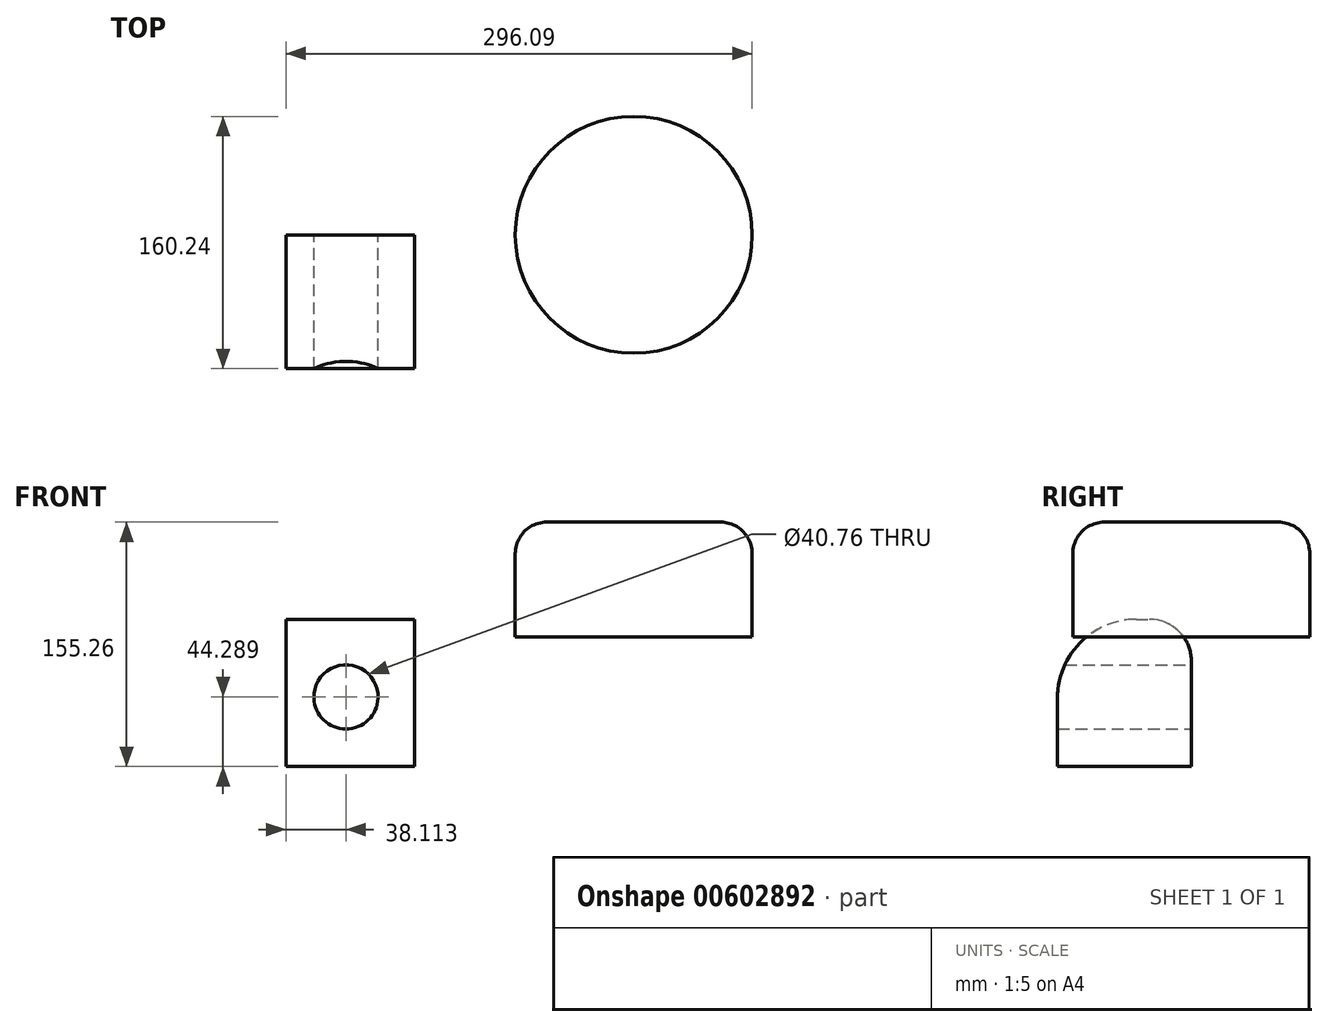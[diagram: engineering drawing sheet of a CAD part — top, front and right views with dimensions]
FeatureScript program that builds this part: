
annotation { "Feature Type Name" : "Feature", "Feature Type Description" : "" }
export const myFeature = defineFeature(function(context is Context, id is Id, definition is map)
    precondition{}
    {
        {
            var Q0;
            Q0=qCreatedBy(makeId("Top.planeOp"),FACE);
            var sketch = newSketch(context, id + "F0", { "sketchPlane" : qUnion([Q0])});
            skCircle(sketch, "E0", {"center": v(0, 0) * mm, "radius": 75.24 * mm});
            skSolve(sketch);
        }
        {
            var Q0;
            Q0=makeQuery(id+"F0.imprint","IMPRINT",FACE,{"disambiguationData":[TD([[makeQuery(id+"F0.imprint","IMPRINT",EDGE,{"derivedFrom":sQuery(id+"F0.wireOp",EDGE,"E0")}),1.0]])]});
            var Q1;
            Q1=sQuery(id+"F0.wireOp",EDGE,"E0");
            extrude(context, id + "F1", {"entities" : qUnion([Q0]), "surfaceEntities" : qUnion([Q1]), "depth" : 73 * mm, "offsetDistance" : 25 * mm});
        }
        {
            var Q0;
            Q0=qCreatedBy(makeId("Front.planeOp"),FACE);
            var sketch = newSketch(context, id + "F2", { "sketchPlane" : qUnion([Q0])});
            skLineSegment(sketch, "E1.bottom", {"start": v(-139.36, 11.27) * mm, "end": v(-220.85, 11.27) * mm});
            skLineSegment(sketch, "E1.top", {"start": v(-139.36, -82.26) * mm, "end": v(-220.85, -82.26) * mm});
            skLineSegment(sketch, "E1.left", {"start": v(-139.36, 11.27) * mm, "end": v(-139.36, -82.26) * mm});
            skLineSegment(sketch, "E1.right", {"start": v(-220.85, 11.27) * mm, "end": v(-220.85, -82.26) * mm});
            skCircle(sketch, "E2", {"center": v(-182.74, -37.97) * mm, "radius": 20.38 * mm});
            skSolve(sketch);
        }
        {
            var Q0;
            Q0=makeQuery(id+"F2.imprint","IMPRINT",FACE,{"disambiguationData":[TD([[makeQuery(id+"F2.imprint","IMPRINT",EDGE,{"derivedFrom":sQuery(id+"F2.wireOp",EDGE,"E1.bottom")}),1.0]])]});
            extrude(context, id + "F3", {"entities" : qUnion([Q0]), "depth" : 85 * mm, "offsetDistance" : 25 * mm});
        }
        {
            var Q0;
            Q0=makeQuery(id+"F3.opExtrude","CAP_EDGE",EDGE,{"disambiguationData":[OSD([sQuery(id+"F2.wireOp",EDGE,"E1.bottom")])],"isStart":false});
            fillet(context, id + "F4", {"entities" : qUnion([Q0]), "radius" : 50 * mm, "tangentPropagation" : true, "allowEdgeOverflow" : false});
        }
        {
            var Q0;
            Q0=makeQuery(id+"F3.opExtrude","CAP_EDGE",EDGE,{"disambiguationData":[OSD([sQuery(id+"F2.wireOp",EDGE,"E1.bottom")])],"isStart":true});
            fillet(context, id + "F5", {"entities" : qUnion([Q0]), "radius" : 26.56 * mm, "tangentPropagation" : true, "allowEdgeOverflow" : false});
        }
        {
            var Q0;
            Q0=makeQuery(id+"F1.opExtrude","CAP_EDGE",EDGE,{"disambiguationData":[OSD([sQuery(id+"F0.wireOp",EDGE,"E0")])],"isStart":false});
            fillet(context, id + "F6", {"entities" : qUnion([Q0]), "radius" : 20 * mm, "tangentPropagation" : true, "allowEdgeOverflow" : false});
        }
    });
